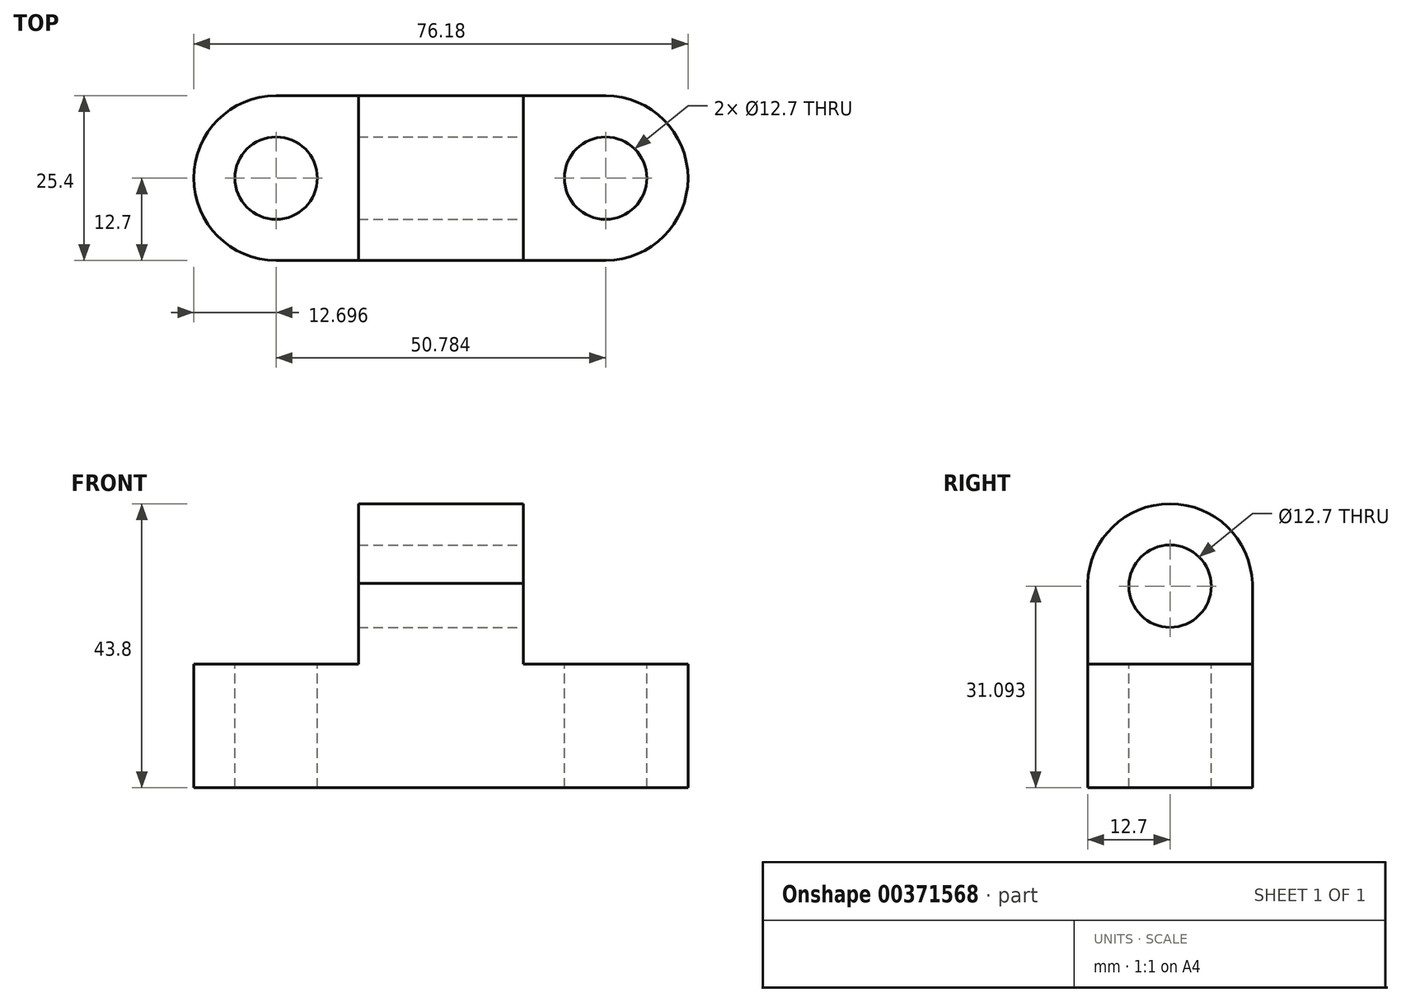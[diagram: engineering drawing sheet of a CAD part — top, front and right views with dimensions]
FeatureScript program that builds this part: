
annotation { "Feature Type Name" : "Feature", "Feature Type Description" : "" }
export const myFeature = defineFeature(function(context is Context, id is Id, definition is map)
    precondition{}
    {
        {
            var Q0;
            Q0=qCreatedBy(makeId("Front.planeOp"),FACE);
            var sketch = newSketch(context, id + "F0", { "sketchPlane" : qUnion([Q0])});
            skLineSegment(sketch, "E0", {"start": v(0, 0) * mm, "end": v(0, 19.05) * mm});
            skLineSegment(sketch, "E1", {"start": v(0, 19.05) * mm, "end": v(25.4, 19.05) * mm});
            skLineSegment(sketch, "E2", {"start": v(25.4, 19.05) * mm, "end": v(25.4, 43.98) * mm});
            skLineSegment(sketch, "E3", {"start": v(25.4, 43.98) * mm, "end": v(50.8, 43.98) * mm});
            skLineSegment(sketch, "E4", {"start": v(50.8, 43.98) * mm, "end": v(50.8, 19.05) * mm});
            skLineSegment(sketch, "E5", {"start": v(50.8, 19.05) * mm, "end": v(76.2, 19.05) * mm});
            skLineSegment(sketch, "E6", {"start": v(76.2, 19.05) * mm, "end": v(76.2, 0) * mm});
            skLineSegment(sketch, "E7", {"start": v(76.2, 0) * mm, "end": v(0, 0) * mm});
            skSolve(sketch);
        }
        {
            var Q0;
            Q0 = qSketchRegion(id + "F0", true);
            extrude(context, id + "F1", {"entities" : qUnion([Q0]), "depth" : 25.4 * mm});
        }
        {
            var Q0;
            Q0=makeQuery(id+"F1.opExtrude","SWEPT_FACE",FACE,{"disambiguationData":[OSD([sQuery(id+"F0.wireOp",EDGE,"E4")])]});
            var sketch = newSketch(context, id + "F2", { "sketchPlane" : qUnion([Q0])});
            skArc(sketch, "E8", {"start": v(0, 31.51) * mm, "mid": v(-12.7, 43.8) * mm, "end": v(-25.4, 31.51) * mm});
            skCircle(sketch, "E9", {"center": v(-12.7, 31.1) * mm, "radius": 6.35 * mm});
            skSolve(sketch);
        }
        {
            var Q0;
            Q0=makeQuery(id+"F2.imprint","IMPRINT",FACE,{"disambiguationData":[TD([[makeQuery(id+"F2.imprint","IMPRINT",EDGE,{"derivedFrom":sQuery(id+"F2.wireOp",EDGE,"E9")}),1.0]])]});
            var Q1;
            {var subQ0=sQuery(id+"F2.wireOp",EDGE,"E8");Q1=makeQuery(id+"F2.imprint","IMPRINT",FACE,{"disambiguationData":[TD([[makeQuery(id+"F2.imprint","IMPRINT",EDGE,{"derivedFrom":subQ0}),-1.0]])]});}
            extrude(context, id + "F3", {"entities" : qUnion([Q0, Q1]), "operationType" : NewBodyOperationType.REMOVE, "oppositeDirection" : true, "depth" : 25.4 * mm});
        }
        {
            var Q0;
            Q0=makeQuery(id+"F1.opExtrude","SWEPT_FACE",FACE,{"disambiguationData":[OSD([sQuery(id+"F0.wireOp",EDGE,"E1")])]});
            var sketch = newSketch(context, id + "F4", { "sketchPlane" : qUnion([Q0])});
            skArc(sketch, "E10", {"start": v(12.7, 0) * mm, "mid": v(0.02, -12.7) * mm, "end": v(12.7, -25.4) * mm});
            skCircle(sketch, "E11", {"center": v(12.72, -12.7) * mm, "radius": 6.35 * mm});
            skCircle(sketch, "E12", {"center": v(63.5, -12.7) * mm, "radius": 6.35 * mm});
            skArc(sketch, "E13", {"start": v(63.5, -25.4) * mm, "mid": v(76.2, -12.7) * mm, "end": v(63.5, 0) * mm});
            skSolve(sketch);
        }
        {
            var Q0;
            Q0=makeQuery(id+"F4.imprint","IMPRINT",FACE,{"disambiguationData":[TD([[makeQuery(id+"F4.imprint","IMPRINT",EDGE,{"derivedFrom":sQuery(id+"F4.wireOp",EDGE,"E11")}),1.0]])]});
            var Q1;
            {var subQ0=sQuery(id+"F4.wireOp",EDGE,"E10");Q1=makeQuery(id+"F4.imprint","IMPRINT",FACE,{"disambiguationData":[TD([[makeQuery(id+"F4.imprint","IMPRINT",EDGE,{"derivedFrom":subQ0}),-1.0]])]});}
            var Q2;
            Q2=makeQuery(id+"F4.imprint","IMPRINT",FACE,{"disambiguationData":[TD([[makeQuery(id+"F4.imprint","IMPRINT",EDGE,{"derivedFrom":sQuery(id+"F4.wireOp",EDGE,"E12")}),1.0]])]});
            extrude(context, id + "F5", {"entities" : qUnion([Q0, Q1, Q2]), "operationType" : NewBodyOperationType.REMOVE, "oppositeDirection" : true, "depth" : 25.4 * mm});
        }
        {
            var Q0;
            Q0=makeQuery(id+"F1.opExtrude","SWEPT_FACE",FACE,{"disambiguationData":[OSD([sQuery(id+"F0.wireOp",EDGE,"E5")])]});
            var sketch = newSketch(context, id + "F6", { "sketchPlane" : qUnion([Q0])});
            skArc(sketch, "E14", {"start": v(63.5, -25.4) * mm, "mid": v(76.2, -12.7) * mm, "end": v(63.5, 0) * mm});
            skSolve(sketch);
        }
        {
            var Q0;
            {var subQ0=sQuery(id+"F6.wireOp",EDGE,"E14");var subQ1=sQuery(id+"F0.wireOp",EDGE,"E5");var subQ2=makeQuery(id+"F1.opExtrude","CAP_EDGE",EDGE,{"disambiguationData":[OSD([subQ1])],"isStart":true});var subQ3=makeQuery(id+"F6.imprint","INTERSECT",VERTEX,{"derivedFrom":[subQ2,subQ0]});Q0=makeQuery(id+"F6.imprint","IMPRINT",FACE,{"disambiguationData":[TD([[makeQuery(id+"F6.imprint","IMPRINT",EDGE,{"disambiguationData":[TD([[subQ3,1.0]])],"derivedFrom":subQ0}),-1.0]])]});}
            var Q1;
            {var subQ0=sQuery(id+"F6.wireOp",EDGE,"E14");var subQ1=sQuery(id+"F0.wireOp",EDGE,"E5");var subQ2=makeQuery(id+"F1.opExtrude","CAP_EDGE",EDGE,{"disambiguationData":[OSD([subQ1])],"isStart":false});var subQ3=makeQuery(id+"F6.imprint","INTERSECT",VERTEX,{"derivedFrom":[subQ2,subQ0]});Q1=makeQuery(id+"F6.imprint","IMPRINT",FACE,{"disambiguationData":[TD([[makeQuery(id+"F6.imprint","IMPRINT",EDGE,{"disambiguationData":[TD([[subQ3,-1.0]])],"derivedFrom":subQ0}),-1.0]])]});}
            extrude(context, id + "F7", {"entities" : qUnion([Q0, Q1]), "operationType" : NewBodyOperationType.REMOVE, "oppositeDirection" : true, "depth" : 25.4 * mm});
        }
    });
